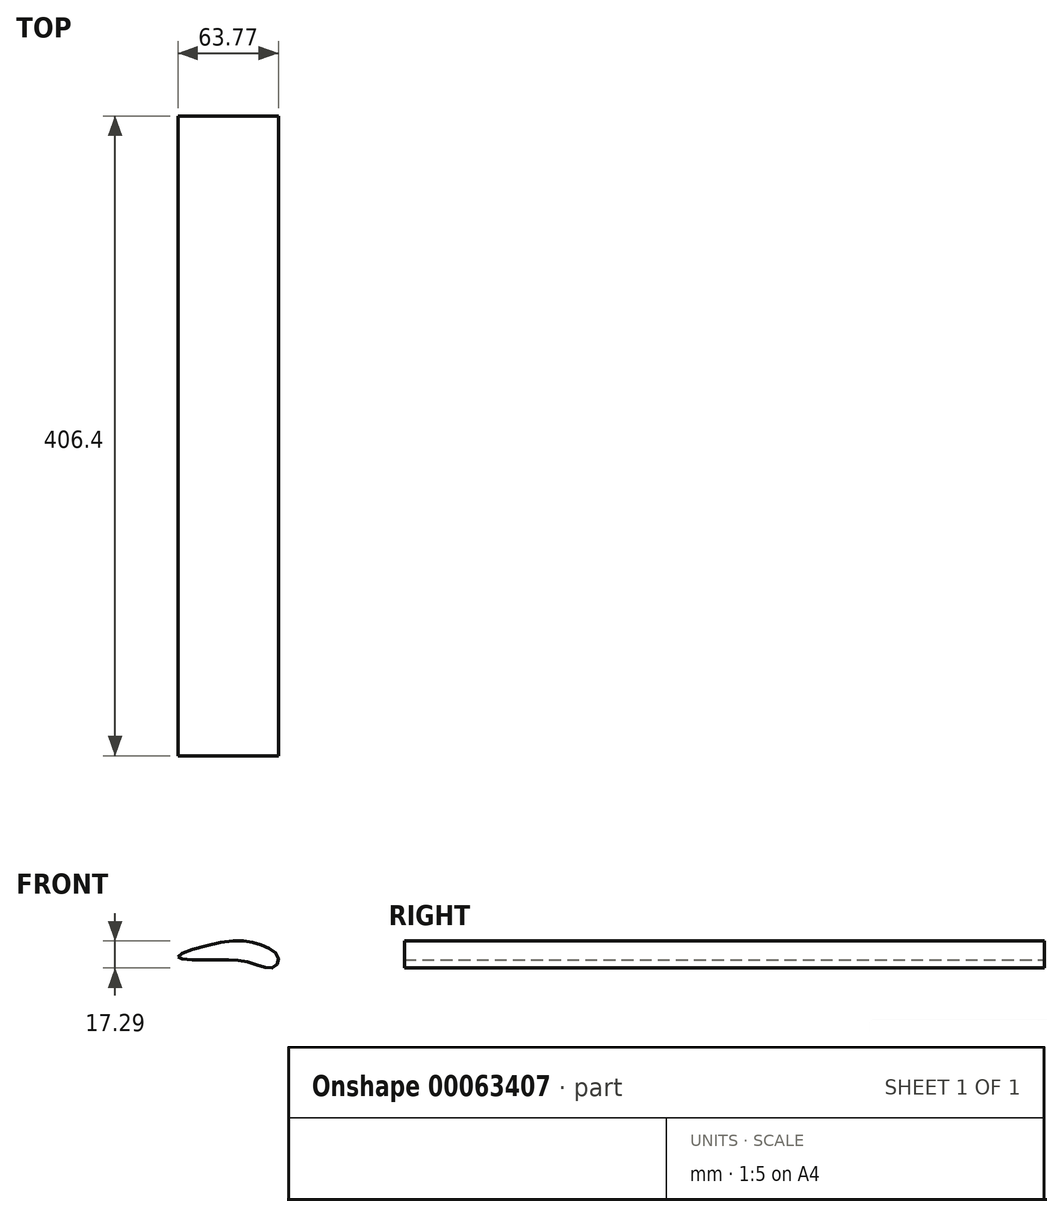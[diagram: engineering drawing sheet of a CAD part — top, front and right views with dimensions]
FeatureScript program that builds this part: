
annotation { "Feature Type Name" : "Feature", "Feature Type Description" : "" }
export const myFeature = defineFeature(function(context is Context, id is Id, definition is map)
    precondition{}
    {
        {
            var Q0;
            Q0=qCreatedBy(makeId("Front.planeOp"),FACE);
            var sketch = newSketch(context, id + "F0", { "sketchPlane" : qUnion([Q0])});
            skFitSpline(sketch, "E0", {"points": [v(0, 0) * mm, v(28.44, 9.25) * mm, v(51.9, 7.87) * mm, v(63.5, 0) * mm, v(60.74, -6.76) * mm, v(45.83, -3.73) * mm, v(21.26, -2.07) * mm, v(0, 0) * mm]});
            skSolve(sketch);
        }
        {
            var Q0;
            Q0 = qSketchRegion(id + "F0", true);
            extrude(context, id + "F1", {"entities" : qUnion([Q0]), "depth" : 406.4 * mm});
        }
    });
